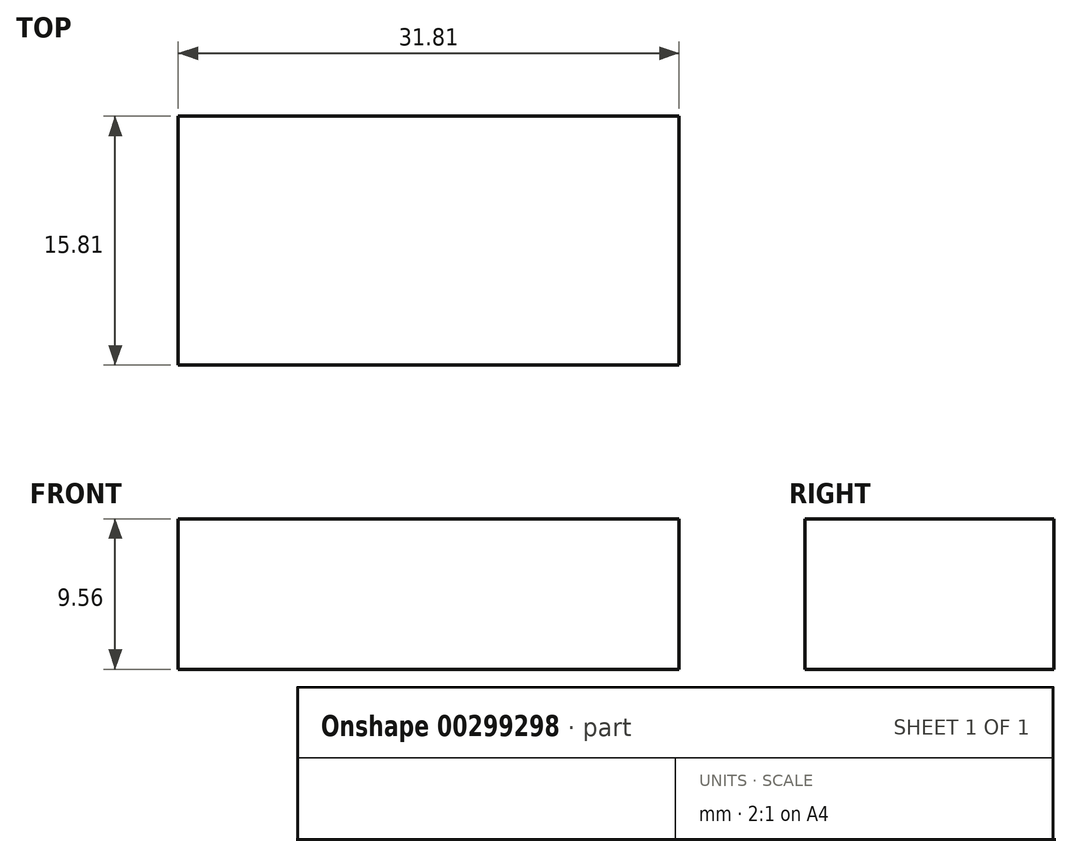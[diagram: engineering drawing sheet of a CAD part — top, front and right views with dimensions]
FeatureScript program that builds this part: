
annotation { "Feature Type Name" : "Feature", "Feature Type Description" : "" }
export const myFeature = defineFeature(function(context is Context, id is Id, definition is map)
    precondition{}
    {
        {
            var Q0;
            Q0=qCreatedBy(makeId("Front.planeOp"),FACE);
            var sketch = newSketch(context, id + "F0", { "sketchPlane" : qUnion([Q0])});
            skLineSegment(sketch, "E0.bottom", {"start": v(-16.4, 4.5) * mm, "end": v(15.41, 4.5) * mm});
            skLineSegment(sketch, "E0.top", {"start": v(-16.4, -5.05) * mm, "end": v(15.41, -5.05) * mm});
            skLineSegment(sketch, "E0.left", {"start": v(-16.4, 4.5) * mm, "end": v(-16.4, -5.05) * mm});
            skLineSegment(sketch, "E0.right", {"start": v(15.41, 4.5) * mm, "end": v(15.41, -5.05) * mm});
            skSolve(sketch);
        }
        {
            var Q0;
            Q0 = qSketchRegion(id + "F0", true);
            extrude(context, id + "F1", {"entities" : qUnion([Q0]), "depth" : 15.8 * mm});
        }
    });
